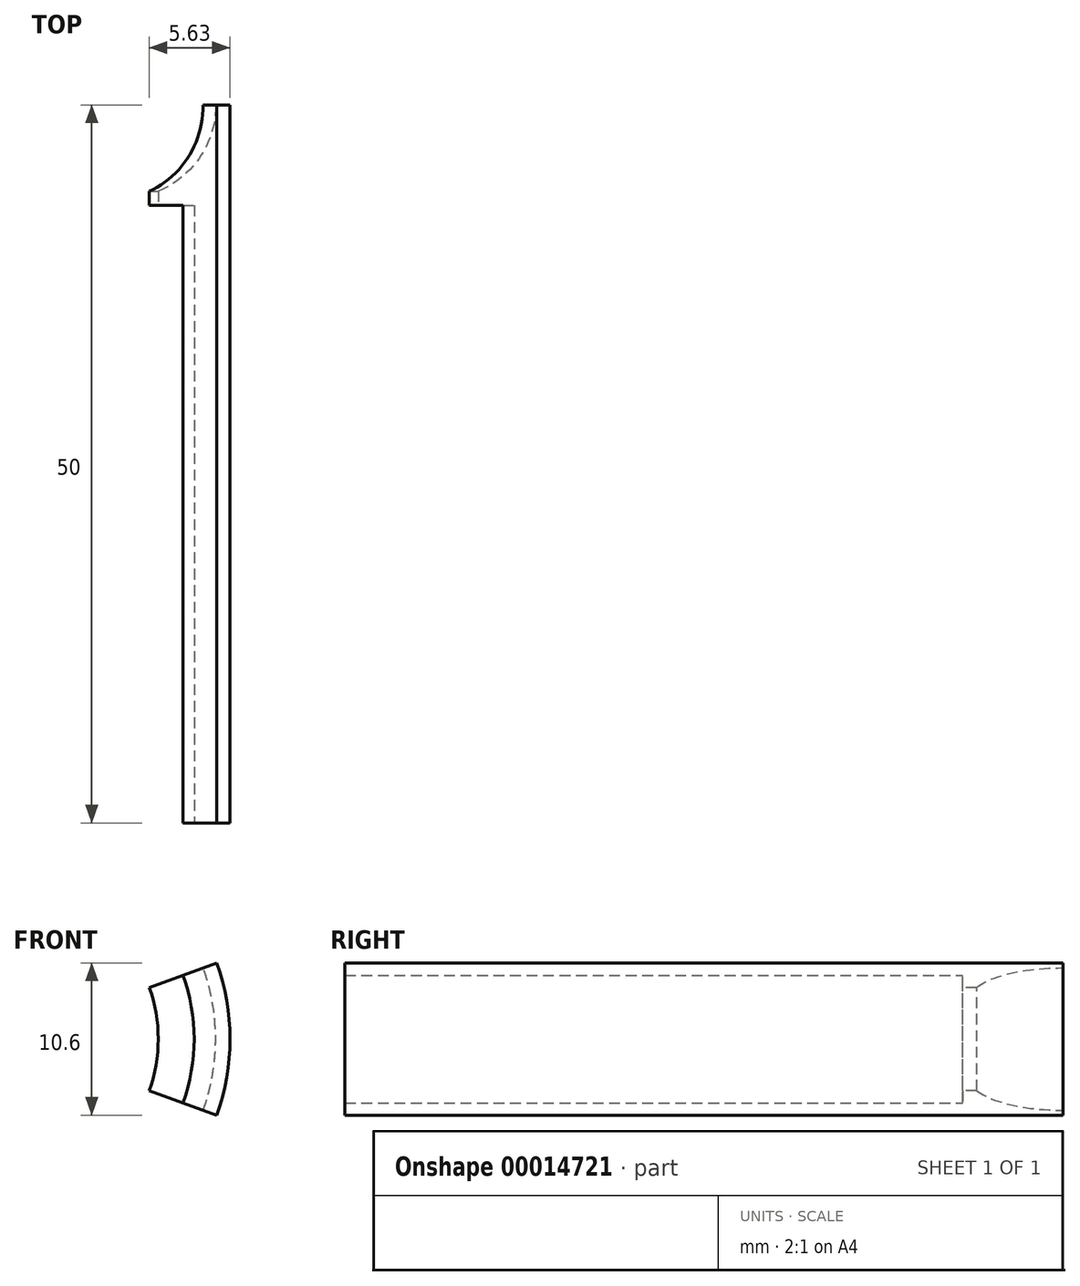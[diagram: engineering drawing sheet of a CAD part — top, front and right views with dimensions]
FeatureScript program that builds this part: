
annotation { "Feature Type Name" : "Feature", "Feature Type Description" : "" }
export const myFeature = defineFeature(function(context is Context, id is Id, definition is map)
    precondition{}
    {
        {
            var Q0;
            Q0=qCreatedBy(makeId("Top.planeOp"),FACE);
            var sketch = newSketch(context, id + "F0", { "sketchPlane" : qUnion([Q0])});
            skLineSegment(sketch, "E0", {"start": v(0, 0) * mm, "end": v(0, -50) * mm});
            skLineSegment(sketch, "E1", {"start": v(0, -50) * mm, "end": v(-2.5, -50) * mm});
            skLineSegment(sketch, "E2", {"start": v(-2.5, -50) * mm, "end": v(-2.5, -6) * mm});
            skLineSegment(sketch, "E3", {"start": v(-1, 0) * mm, "end": v(0, 0) * mm});
            skLineSegment(sketch, "E4", {"start": v(-2.5, -6) * mm, "end": v(-5, -6) * mm});
            skLineSegment(sketch, "E5", {"start": v(-15.5, -42.55) * mm, "end": v(-15.5, 2.52) * mm, "construction": true});
            skLineSegment(sketch, "E6", {"start": v(-5, -6) * mm, "end": v(-5, -7) * mm});
            skLineSegment(sketch, "E7", {"start": v(-5, -7) * mm, "end": v(-2.5, -7) * mm});
            skArc(sketch, "E8", {"start": v(-5, -6) * mm, "mid": v(-2.08, -3.61) * mm, "end": v(-1, 0) * mm});
            skSolve(sketch);
        }
        {
            var Q0;
            Q0 = qSketchRegion(id + "F0", true);
            var Q1;
            Q1=sQuery(id+"F0.wireOp",EDGE,"E5");
            revolve(context, id + "F1", {"entities" : qUnion([Q0]), "axis" : qUnion([Q1]), "revolveType" : RevolveType.TWO_DIRECTIONS, "angle" : 20 * degree, "angleBack" : 340 * degree});
        }
    });
